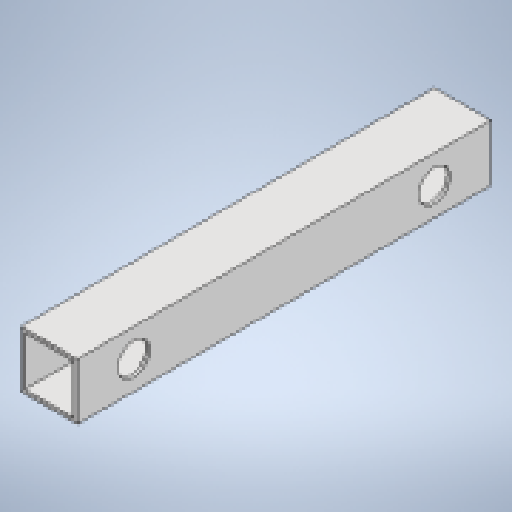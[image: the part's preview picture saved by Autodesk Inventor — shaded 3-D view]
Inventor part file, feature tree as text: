
AUTODESK INVENTOR PART (.ipt)
format: ipt  version: 2025.1 (Build 291241020, 241B)  size: 188,928 bytes
history: native  units: mm
features: extrude x2, sketch x2, projected_geometry x1
ambient origin geometry x8: Origin, YZ Plane, XZ Plane, XY Plane, X Axis, Y Axis, Z Axis, Center Point
bodies: Body1 (feature_tree)
feature tree (5):
  extrude  "Extrusion3"  Depth=30.0mm
  extrude  "Extrusion4"  Depth=2.0mm
  sketch  "Sketch9"  dims[d61=500.0mm d172=30.0mm]
  sketch  "Sketch10"  dims[d173=30.0mm d174=2.0mm d175=220.0mm d176=0.0mm d177=17.0mm d178=17.0mm d179=0.0mm d180=0.0mm d181=30.0mm d182=90.0mm d183=220.0mm d184=450.0mm d185=500.0mm d186=17.0mm]
  projected_geometry  "Projected Loop3"
